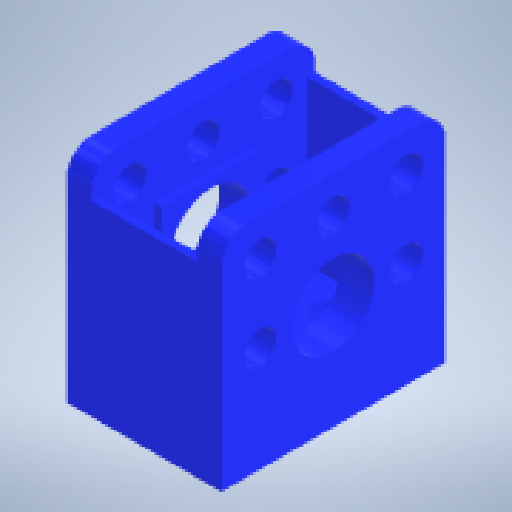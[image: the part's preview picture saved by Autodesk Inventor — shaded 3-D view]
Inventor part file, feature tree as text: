
AUTODESK INVENTOR PART (.ipt)
format: ipt  version: 2023.1 (Build 271208000, 208)  size: 358,400 bytes
history: native  units: mm
features: sketch x8, extrude x7, fillet x1, hole x1
ambient origin geometry x8: Origin, YZ Plane, XZ Plane, XY Plane, X Axis, Y Axis, Z Axis, Center Point
bodies: Solid1 (feature_tree)
feature tree (17):
  extrude  "Extrusion1"  Depth=27.5mm
  extrude  "Extrusion2"  Depth=9.5mm
  extrude  "Extrusion3"  Depth=3.0mm
  fillet  "Fillet1"  Radius=3.0mm
  extrude  "Extrusion4"  Depth=1.0mm
  hole  "Hole1"  [1 undecoded]
  extrude  "Extrusion5"  Depth=3.0mm
  extrude  "Extrusion6"  Depth=4.0mm
  extrude  "Extrusion7"  Depth=9.0mm
  sketch  "Sketch1"  dims[d0=19.0mm d1=27.5mm]
  sketch  "Sketch2"  dims[d2=13.75mm d3=9.5mm]
  sketch  "Sketch3"  dims[d4=27.0mm d5=0.0mm d6=3.0mm d7=3.0mm]
  sketch  "Sketch4"  dims[d8=1.0mm d9=1.0mm]
  sketch  "Sketch5"  dims[d10=24.0mm d11=0.0mm d12=4.0mm]
  sketch  "Sketch6"  dims[d13=30.0mm d14=0.0mm d15=3.0mm]
  sketch  "Sketch7"  dims[d16=4.0mm d17=4.0mm]
  sketch  "Sketch8"  dims[d18=4.0mm d19=9.0mm d20=9.0mm d21=5.0mm d22=0.0mm d23=14.0mm d24=27.5mm d25=13.75mm d26=4.0mm d27=0.0mm d28=0.0mm d29=4.0mm d30=4.0mm d31=9.0mm d32=9.0mm d35=4.75mm d36=4.0mm d37=6.0mm d38=4.0mm d39=2.0mm d40=90.0deg d41=8.0mm d42=20.594885mm d43=12.0mm d44=12.0mm d45=6.0mm d46=6.0mm d47=1.0mm d48=0.0mm d49=1.0mm d50=0.0mm d51=10.0mm d52=0.0mm d53=0.0mm]
note: 1 required parameter value undecoded (feature->parameter linkage not recoverable at this tier; creation-order binding heuristic only, values carry confidence <= 0.55)
